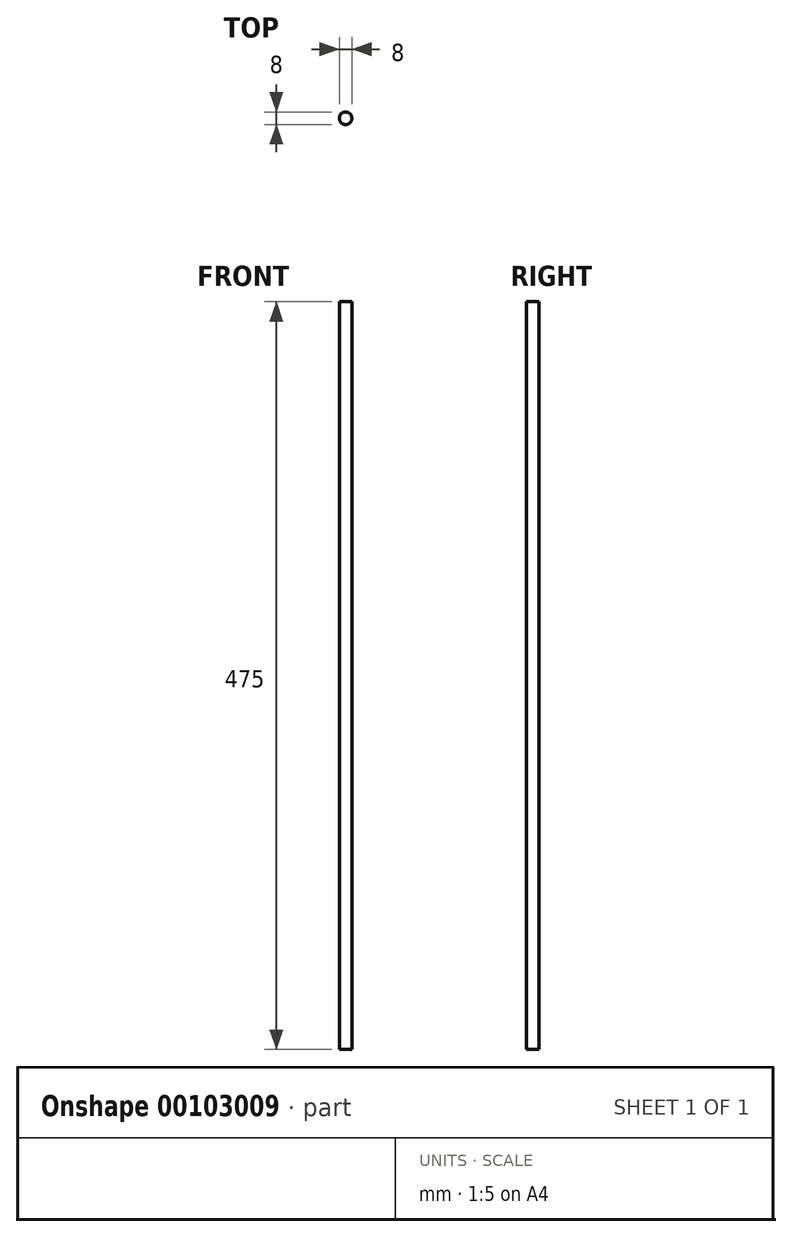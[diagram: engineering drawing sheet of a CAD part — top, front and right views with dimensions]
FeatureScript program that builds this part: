
annotation { "Feature Type Name" : "Feature", "Feature Type Description" : "" }
export const myFeature = defineFeature(function(context is Context, id is Id, definition is map)
    precondition{}
    {
        {
            var Q0;
            Q0=qCreatedBy(makeId("Top.planeOp"),FACE);
            var sketch = newSketch(context, id + "F0", { "sketchPlane" : qUnion([Q0])});
            skCircle(sketch, "E0", {"center": v(0, 0) * mm, "radius": 4 * mm});
            skSolve(sketch);
        }
        {
            var Q0;
            Q0=qSketchRegion(id+"F0",true);
            extrude(context, id + "F1", {"entities" : qUnion([Q0]), "depth" : 475 * mm});
        }
    });
